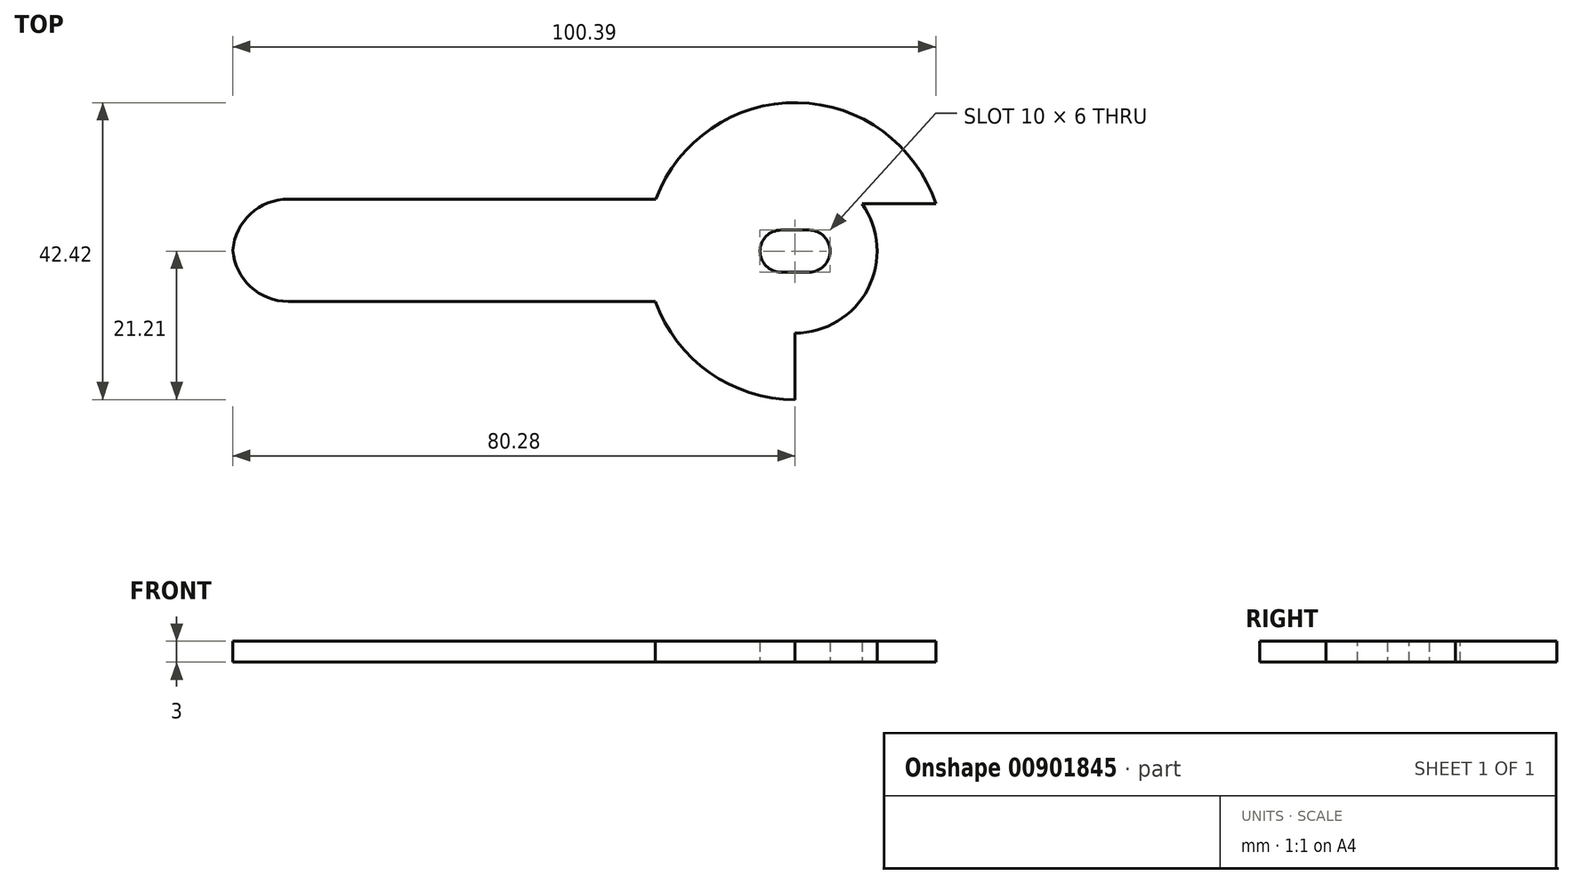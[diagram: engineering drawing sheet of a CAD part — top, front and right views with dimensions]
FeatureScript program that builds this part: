
annotation { "Feature Type Name" : "Feature", "Feature Type Description" : "" }
export const myFeature = defineFeature(function(context is Context, id is Id, definition is map)
    precondition{}
    {
        {
            var Q0;
            Q0=qCreatedBy(makeId("Top.planeOp"),FACE);
            var sketch = newSketch(context, id + "F0", { "sketchPlane" : qUnion([Q0])});
            skArc(sketch, "E0", {"start": v(20.11, 6.74) * mm, "mid": v(-17.22, 12.39) * mm, "end": v(0, -21.21) * mm});
            skLineSegment(sketch, "E1", {"start": v(0, -21.21) * mm, "end": v(0, -11.71) * mm});
            skLineSegment(sketch, "E2", {"start": v(-2, -3) * mm, "end": v(2, -3) * mm});
            skLineSegment(sketch, "E3", {"start": v(-2, 3) * mm, "end": v(2, 3) * mm});
            skArc(sketch, "E4", {"start": v(-2, 3) * mm, "mid": v(-5, 0) * mm, "end": v(-2, -3) * mm});
            skArc(sketch, "E5", {"start": v(2, 3) * mm, "mid": v(5, 0) * mm, "end": v(2, -3) * mm});
            skLineSegment(sketch, "E6", {"start": v(20.11, 6.74) * mm, "end": v(9.58, 6.74) * mm});
            skPoint(sketch, "E7.orphan", {"position": v(21.21, 0) * mm});
            skArc(sketch, "E8", {"start": v(0, -11.71) * mm, "mid": v(10.4, -5.4) * mm, "end": v(9.58, 6.74) * mm});
            skSolve(sketch);
        }
        {
            var Q0;
            Q0 = qSketchRegion(id + "F0", true);
            extrude(context, id + "F1", {"entities" : qUnion([Q0]), "depth" : 3 * mm, "offsetDistance" : 25 * mm, "symmetric" : true});
        }
        {
            var Q0;
            Q0=makeQuery(id+"F1.opExtrude","CAP_FACE",FACE,{"disambiguationData":[OSD([sQuery(id+"F0.wireOp",EDGE,"E0"),sQuery(id+"F0.wireOp",EDGE,"Zk3O90I3-Ipmq-YTcO-4mlO-qnDephtRHMpm"),sQuery(id+"F0.wireOp",EDGE,"E1"),sQuery(id+"F0.wireOp",EDGE,"8lkZdH2R-5fk8-27cL-mLQG-GSOhsJiB4Zd0"),sQuery(id+"F0.wireOp",EDGE,"L11yh7N8-bkZs-kFin-OZ5n-GATUcH6lFuI5")])],"isStart":false});
            var sketch = newSketch(context, id + "F2", { "sketchPlane" : qUnion([Q0])});
            skLineSegment(sketch, "E9", {"start": v(-19.87, 7.43) * mm, "end": v(-80.3, 7.43) * mm});
            skLineSegment(sketch, "E10", {"start": v(-80.3, 7.43) * mm, "end": v(-80.3, -7.2) * mm});
            skLineSegment(sketch, "E11", {"start": v(-80.3, -7.2) * mm, "end": v(-19.95, -7.2) * mm});
            skLineSegment(sketch, "E12", {"start": v(-19.87, 7.43) * mm, "end": v(-19.95, -7.2) * mm});
            skSolve(sketch);
        }
        {
            var Q0;
            {var subQ0=sQuery(id+"F2.wireOp",EDGE,"E9");Q0=makeQuery(id+"F2.imprint","IMPRINT",FACE,{"disambiguationData":[TD([[makeQuery(id+"F2.imprint","IMPRINT",EDGE,{"derivedFrom":subQ0}),1.0]])]});}
            extrude(context, id + "F3", {"entities" : qUnion([Q0]), "operationType" : NewBodyOperationType.ADD, "oppositeDirection" : true, "depth" : 3 * mm, "offsetDistance" : 25 * mm});
        }
        {
            var Q0;
            Q0=makeQuery(id+"F3.opExtrude","SWEPT_EDGE",EDGE,{"disambiguationData":[OSD([sQuery(id+"F2.wireOp",EDGE,"E10"),sQuery(id+"F2.wireOp",EDGE,"E11")])]});
            var Q1;
            Q1=makeQuery(id+"F3.opExtrude","SWEPT_EDGE",EDGE,{"disambiguationData":[OSD([sQuery(id+"F2.wireOp",EDGE,"E9"),sQuery(id+"F2.wireOp",EDGE,"E10")])]});
            fillet(context, id + "F4", {"entities" : qUnion([Q0, Q1]), "radius" : 7.97 * mm, "tangentPropagation" : true, "allowEdgeOverflow" : false});
        }
    });
